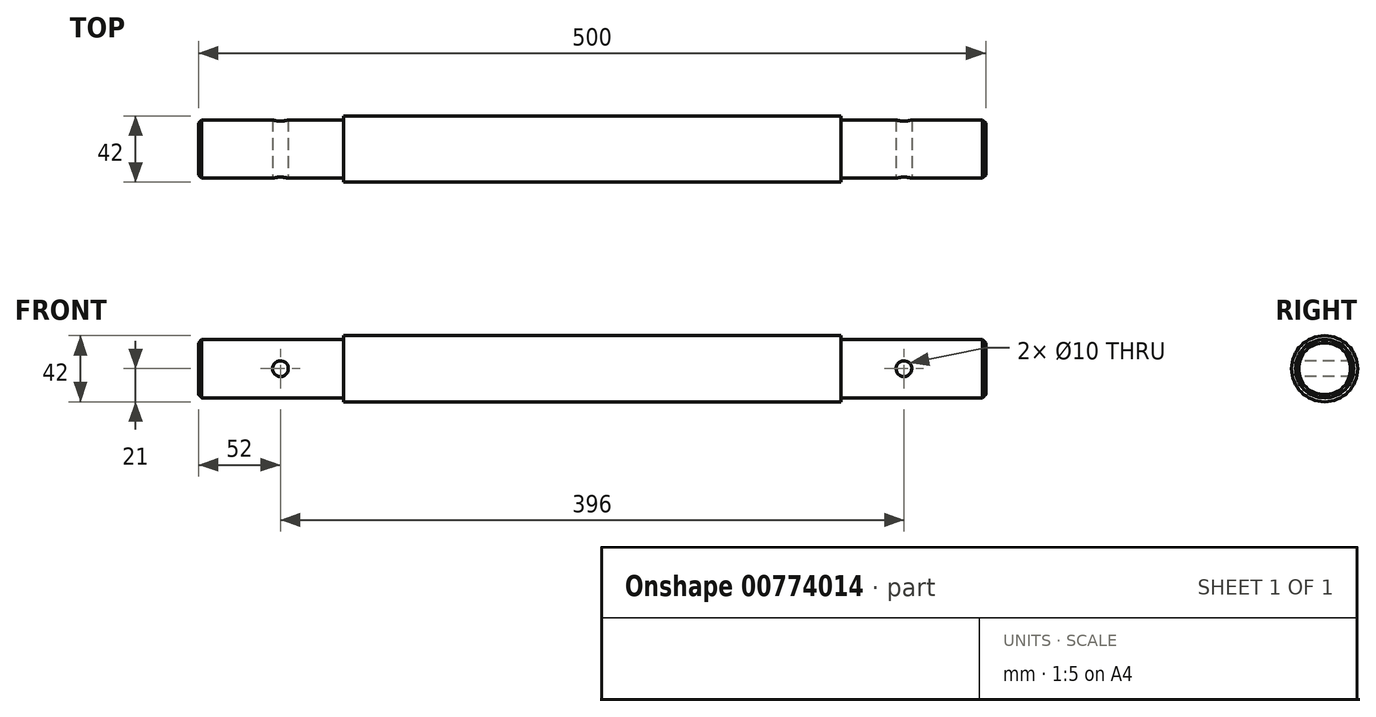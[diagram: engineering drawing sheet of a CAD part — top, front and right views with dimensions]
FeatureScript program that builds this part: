
annotation { "Feature Type Name" : "Feature", "Feature Type Description" : "" }
export const myFeature = defineFeature(function(context is Context, id is Id, definition is map)
    precondition{}
    {
        {
            var Q0;
            Q0=qCreatedBy(makeId("Right.planeOp"),FACE);
            var sketch = newSketch(context, id + "F0", { "sketchPlane" : qUnion([Q0])});
            skCircle(sketch, "E0", {"center": v(0, 0) * mm, "radius": 21 * mm});
            skCircle(sketch, "E1", {"center": v(0, 0) * mm, "radius": 18.5 * mm});
            skSolve(sketch);
        }
        {
            var Q0;
            Q0=makeQuery(id+"F0.imprint","IMPRINT",FACE,{"disambiguationData":[TD([[makeQuery(id+"F0.imprint","IMPRINT",EDGE,{"derivedFrom":sQuery(id+"F0.wireOp",EDGE,"E1")}),1.0]])]});
            extrude(context, id + "F1", {"entities" : qUnion([Q0]), "depth" : 500 * mm, "offsetDistance" : 25 * mm, "symmetric" : true});
        }
        {
            var Q0;
            Q0=makeQuery(id+"F0.imprint","IMPRINT",FACE,{"disambiguationData":[TD([[makeQuery(id+"F0.imprint","IMPRINT",EDGE,{"derivedFrom":sQuery(id+"F0.wireOp",EDGE,"E0")}),1.0]])]});
            extrude(context, id + "F2", {"entities" : qUnion([Q0]), "operationType" : NewBodyOperationType.ADD, "depth" : 316 * mm, "offsetDistance" : 25 * mm, "symmetric" : true});
        }
        {
            var Q0;
            Q0=makeQuery(id+"F1.opExtrude","CAP_EDGE",EDGE,{"disambiguationData":[OSD([sQuery(id+"F0.wireOp",EDGE,"E1")])],"isStart":false});
            var Q1;
            Q1=makeQuery(id+"F1.opExtrude","CAP_EDGE",EDGE,{"disambiguationData":[OSD([sQuery(id+"F0.wireOp",EDGE,"E1")])],"isStart":true});
            chamfer(context, id + "F3", {"entities" : qUnion([Q0, Q1]), "width" : 2 * mm, "tangentPropagation" : true});
        }
        {
            var Q0;
            Q0=makeQuery(id+"F2.opExtrude","SWEPT_FACE",FACE,{"disambiguationData":[OSD([sQuery(id+"F0.wireOp",EDGE,"E0")])]});
            cPlane(context, id + "F4", {"entities" : qUnion([Q0]), "cplaneType" : CPlaneType.LINE_ANGLE, "offset" : 25 * mm, "angle" : 0 * degree, "width" : 150 * mm, "height" : 150 * mm});
        }
        {
            var Q0;
            Q0=qCreatedBy(id+"F4.planeOp",FACE);
            var sketch = newSketch(context, id + "F5", { "sketchPlane" : qUnion([Q0])});
            skLineSegment(sketch, "E2", {"start": v(0, 0) * mm, "end": v(-198, 0) * mm, "construction": true});
            skCircle(sketch, "E3", {"center": v(-198, 0) * mm, "radius": 5 * mm});
            skLineSegment(sketch, "E4", {"start": v(0, 0) * mm, "end": v(0, 77.97) * mm, "construction": true});
            skCircle(sketch, "E5.MirrorC", {"center": v(198, 0) * mm, "radius": 5 * mm});
            skLineSegment(sketch, "E6.MirrorCS", {"start": v(0, 0) * mm, "end": v(198, 0) * mm, "construction": true});
            skSolve(sketch);
        }
        {
            var Q0;
            Q0 = qSketchRegion(id + "F5", true);
            extrude(context, id + "F6", {"entities" : qUnion([Q0]), "operationType" : NewBodyOperationType.REMOVE, "oppositeDirection" : true, "depth" : 100 * mm, "offsetDistance" : 25 * mm, "symmetric" : true});
        }
    });
